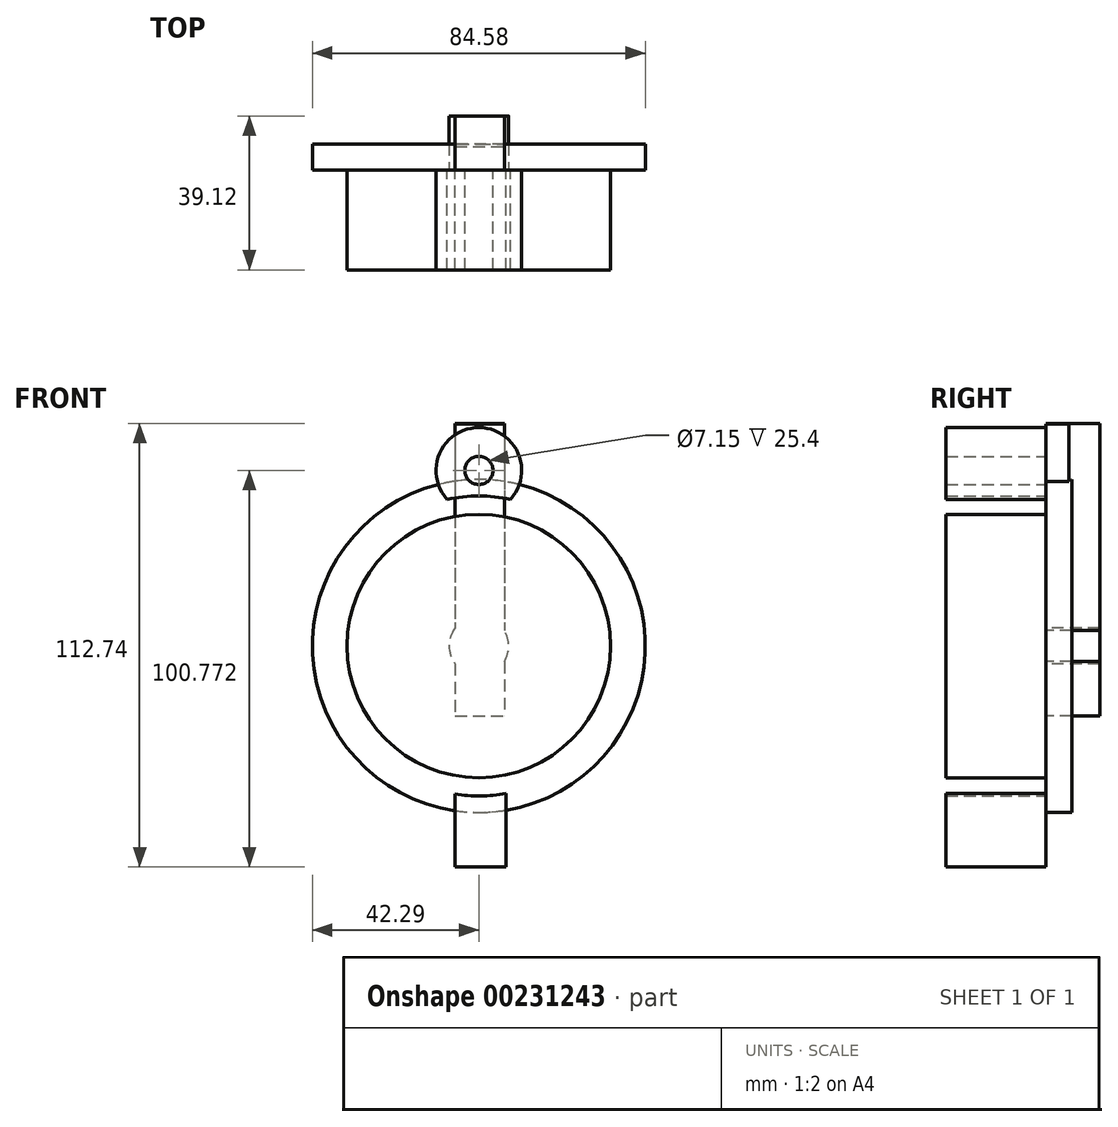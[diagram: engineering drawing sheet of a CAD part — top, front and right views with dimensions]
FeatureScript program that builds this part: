
annotation { "Feature Type Name" : "Feature", "Feature Type Description" : "" }
export const myFeature = defineFeature(function(context is Context, id is Id, definition is map)
    precondition{}
    {
        {
            var Q0;
            Q0=qCreatedBy(makeId("Front.planeOp"),FACE);
            var sketch = newSketch(context, id + "F0", { "sketchPlane" : qUnion([Q0])});
            skCircle(sketch, "E0", {"center": v(0, 0) * mm, "radius": 38.1 * mm});
            skLineSegment(sketch, "E1.bottom", {"start": v(-6.06, 0) * mm, "end": v(6.87, 0) * mm});
            skLineSegment(sketch, "E1.top", {"start": v(-6.06, -56.17) * mm, "end": v(6.87, -56.17) * mm});
            skLineSegment(sketch, "E1.left", {"start": v(-6.06, 0) * mm, "end": v(-6.06, -56.17) * mm});
            skLineSegment(sketch, "E1.right", {"start": v(6.87, 0) * mm, "end": v(6.87, -56.17) * mm});
            skCircle(sketch, "E2", {"center": v(0, 0) * mm, "radius": 33.47 * mm});
            skLineSegment(sketch, "E3", {"start": v(-8.63, 37.11) * mm, "end": v(-3.4, 33.3) * mm});
            skLineSegment(sketch, "E4", {"start": v(-3.4, 33.3) * mm, "end": v(0, 38.1) * mm});
            skLineSegment(sketch, "E5", {"start": v(0, 38.1) * mm, "end": v(4.36, 33.18) * mm});
            skLineSegment(sketch, "E6", {"start": v(4.36, 33.18) * mm, "end": v(8.75, 37.08) * mm});
            skLineSegment(sketch, "E7", {"start": v(8.75, 37.08) * mm, "end": v(10.73, 31.7) * mm});
            skLineSegment(sketch, "E8", {"start": v(10.73, 31.7) * mm, "end": v(17.4, 33.9) * mm});
            skLineSegment(sketch, "E9", {"start": v(17.4, 33.9) * mm, "end": v(17.4, 28.59) * mm});
            skLineSegment(sketch, "E10", {"start": v(17.4, 28.59) * mm, "end": v(25.19, 28.59) * mm});
            skLineSegment(sketch, "E11", {"start": v(25.19, 28.59) * mm, "end": v(23.61, 23.72) * mm});
            skLineSegment(sketch, "E12", {"start": v(23.61, 23.72) * mm, "end": v(29.81, 23.72) * mm});
            skLineSegment(sketch, "E13", {"start": v(29.81, 23.72) * mm, "end": v(27.87, 18.53) * mm});
            skLineSegment(sketch, "E14", {"start": v(27.87, 18.53) * mm, "end": v(33.29, 18.53) * mm});
            skLineSegment(sketch, "E15", {"start": v(33.29, 18.53) * mm, "end": v(30.33, 14.15) * mm});
            skLineSegment(sketch, "E16", {"start": v(30.33, 14.15) * mm, "end": v(36.34, 11.45) * mm});
            skLineSegment(sketch, "E17", {"start": v(36.34, 11.45) * mm, "end": v(32.68, 7.23) * mm});
            skLineSegment(sketch, "E18", {"start": v(32.68, 7.23) * mm, "end": v(37.97, 3.17) * mm});
            skLineSegment(sketch, "E19", {"start": v(37.97, 3.17) * mm, "end": v(33.47, 0) * mm});
            skLineSegment(sketch, "E20", {"start": v(33.47, 0) * mm, "end": v(37.64, -5.92) * mm});
            skLineSegment(sketch, "E21", {"start": v(37.64, -5.92) * mm, "end": v(32.6, -7.57) * mm});
            skLineSegment(sketch, "E22", {"start": v(32.6, -7.57) * mm, "end": v(36.02, -12.42) * mm});
            skLineSegment(sketch, "E23", {"start": v(36.02, -12.42) * mm, "end": v(30.26, -14.3) * mm});
            skLineSegment(sketch, "E24", {"start": v(30.26, -14.3) * mm, "end": v(32.23, -20.32) * mm});
            skLineSegment(sketch, "E25", {"start": v(32.23, -20.32) * mm, "end": v(26.6, -20.32) * mm});
            skLineSegment(sketch, "E26", {"start": v(26.6, -20.32) * mm, "end": v(26.6, -27.28) * mm});
            skLineSegment(sketch, "E27", {"start": v(26.6, -27.28) * mm, "end": v(21.3, -25.81) * mm});
            skLineSegment(sketch, "E28", {"start": v(21.3, -25.81) * mm, "end": v(21.3, -31.58) * mm});
            skLineSegment(sketch, "E29", {"start": v(21.3, -31.58) * mm, "end": v(17.4, -28.59) * mm});
            skLineSegment(sketch, "E30", {"start": v(17.4, -28.59) * mm, "end": v(14.09, -35.4) * mm});
            skLineSegment(sketch, "E31", {"start": v(14.09, -35.4) * mm, "end": v(11.33, -31.5) * mm});
            skLineSegment(sketch, "E32", {"start": v(11.33, -31.5) * mm, "end": v(8.95, -37.03) * mm});
            skLineSegment(sketch, "E33", {"start": v(8.95, -37.03) * mm, "end": v(4.49, -33.17) * mm});
            skLineSegment(sketch, "E34", {"start": v(4.49, -33.17) * mm, "end": v(0, -38.1) * mm});
            skLineSegment(sketch, "E35", {"start": v(0, -38.1) * mm, "end": v(-2.87, -33.35) * mm});
            skLineSegment(sketch, "E36", {"start": v(-2.87, -33.35) * mm, "end": v(-8.31, -37.18) * mm});
            skLineSegment(sketch, "E37", {"start": v(-8.31, -37.18) * mm, "end": v(-10.03, -31.93) * mm});
            skLineSegment(sketch, "E38", {"start": v(-10.03, -31.93) * mm, "end": v(-14.64, -35.17) * mm});
            skLineSegment(sketch, "E39", {"start": v(-14.64, -35.17) * mm, "end": v(-14.64, -30.1) * mm});
            skLineSegment(sketch, "E40", {"start": v(-14.64, -30.1) * mm, "end": v(-20.6, -32.05) * mm});
            skLineSegment(sketch, "E41", {"start": v(-20.6, -32.05) * mm, "end": v(-20.6, -26.38) * mm});
            skLineSegment(sketch, "E42", {"start": v(-20.6, -26.38) * mm, "end": v(-25.76, -28.07) * mm});
            skLineSegment(sketch, "E43", {"start": v(-25.76, -28.07) * mm, "end": v(-25.76, -21.37) * mm});
            skLineSegment(sketch, "E44", {"start": v(-25.76, -21.37) * mm, "end": v(-31.54, -21.37) * mm});
            skLineSegment(sketch, "E45", {"start": v(-31.54, -21.37) * mm, "end": v(-29.5, -15.83) * mm});
            skLineSegment(sketch, "E46", {"start": v(-29.5, -15.83) * mm, "end": v(-35.31, -14.3) * mm});
            skLineSegment(sketch, "E47", {"start": v(-35.31, -14.3) * mm, "end": v(-32.14, -9.34) * mm});
            skLineSegment(sketch, "E48", {"start": v(-32.14, -9.34) * mm, "end": v(-37.69, -5.6) * mm});
            skLineSegment(sketch, "E49", {"start": v(-37.69, -5.6) * mm, "end": v(-33.37, -2.57) * mm});
            skLineSegment(sketch, "E50", {"start": v(-33.37, -2.57) * mm, "end": v(-38.06, 1.63) * mm});
            skLineSegment(sketch, "E51", {"start": v(-38.06, 1.63) * mm, "end": v(-33.07, 5.15) * mm});
            skLineSegment(sketch, "E52", {"start": v(-33.07, 5.15) * mm, "end": v(-36.69, 10.28) * mm});
            skLineSegment(sketch, "E53", {"start": v(-36.69, 10.28) * mm, "end": v(-31.22, 12.08) * mm});
            skLineSegment(sketch, "E54", {"start": v(-31.22, 12.08) * mm, "end": v(-34.34, 16.5) * mm});
            skLineSegment(sketch, "E55", {"start": v(-34.34, 16.5) * mm, "end": v(-27.8, 18.65) * mm});
            skLineSegment(sketch, "E56", {"start": v(-27.8, 18.65) * mm, "end": v(-30.62, 22.67) * mm});
            skLineSegment(sketch, "E57", {"start": v(-30.62, 22.67) * mm, "end": v(-24.62, 22.67) * mm});
            skLineSegment(sketch, "E58", {"start": v(-24.62, 22.67) * mm, "end": v(-24.62, 29.08) * mm});
            skLineSegment(sketch, "E59", {"start": v(-24.62, 29.08) * mm, "end": v(-16.58, 29.08) * mm});
            skLineSegment(sketch, "E60", {"start": v(-16.58, 29.08) * mm, "end": v(-14.65, 35.17) * mm});
            skLineSegment(sketch, "E61", {"start": v(-14.65, 35.17) * mm, "end": v(-11.9, 31.28) * mm});
            skLineSegment(sketch, "E62", {"start": v(-11.9, 31.28) * mm, "end": v(-8.63, 37.11) * mm});
            skPoint(sketch, "E63.end.orphan", {"position": v(-5.46, 44.25) * mm});
            skPoint(sketch, "E64.end.orphan", {"position": v(6.93, 44.25) * mm});
            skCircle(sketch, "E65", {"center": v(0, 44.6) * mm, "radius": 10.9 * mm});
            skCircle(sketch, "E66", {"center": v(0, 44.6) * mm, "radius": 3.58 * mm});
            skSolve(sketch);
        }
        {
            var Q0;
            {var subQ5=sQuery(id+"F0.wireOp",EDGE,"E1.top");Q0=makeQuery(id+"F0.imprint","IMPRINT",FACE,{"disambiguationData":[TD([[makeQuery(id+"F0.imprint","IMPRINT",EDGE,{"derivedFrom":subQ5}),1.0]])]});}
            var Q1;
            {var subQ5=sQuery(id+"F0.wireOp",EDGE,"E1.bottom");Q1=makeQuery(id+"F0.imprint","IMPRINT",FACE,{"disambiguationData":[TD([[makeQuery(id+"F0.imprint","IMPRINT",EDGE,{"derivedFrom":subQ5}),-1.0]])]});}
            var Q2;
            {var subQ5=sQuery(id+"F0.wireOp",EDGE,"E1.bottom");Q2=makeQuery(id+"F0.imprint","IMPRINT",FACE,{"disambiguationData":[TD([[makeQuery(id+"F0.imprint","IMPRINT",EDGE,{"derivedFrom":subQ5}),1.0]])]});}
            var Q3;
            Q3=makeQuery(id+"F0.imprint","IMPRINT",FACE,{"disambiguationData":[TD([[makeQuery(id+"F0.imprint","IMPRINT",EDGE,{"derivedFrom":sQuery(id+"F0.wireOp",EDGE,"CHmG4rNv-3Th5-Iquq-n78B-wOcN8oiSMWzU")}),1.0]])]});
            var Q4;
            {var subQ0=sQuery(id+"F0.wireOp",EDGE,"E0");var subQ2=sQuery(id+"F0.wireOp",EDGE,"E65");var subQ3=makeQuery(id+"F0.imprint","INTERSECT",VERTEX,{"disambiguationData":[OD(0.0)],"derivedFrom":[subQ0,subQ2]});Q4=makeQuery(id+"F0.imprint","IMPRINT",FACE,{"disambiguationData":[TD([[makeQuery(id+"F0.imprint","IMPRINT",EDGE,{"disambiguationData":[TD([[subQ3,-1.0]])],"derivedFrom":subQ2}),1.0]])]});}
            extrude(context, id + "F1", {"entities" : qUnion([Q0, Q1, Q2, Q3, Q4]), "depth" : 25.4 * mm});
        }
        {
            var Q0;
            Q0=qCreatedBy(makeId("Front.planeOp"),FACE);
            var sketch = newSketch(context, id + "F2", { "sketchPlane" : qUnion([Q0])});
            skCircle(sketch, "E67", {"center": v(0, 0) * mm, "radius": 42.29 * mm});
            skLineSegment(sketch, "E68.bottom", {"start": v(5.44, 41.94) * mm, "end": v(-4.85, 41.94) * mm});
            skLineSegment(sketch, "E68.top", {"start": v(5.44, 15.15) * mm, "end": v(-4.85, 15.15) * mm});
            skLineSegment(sketch, "E68.left", {"start": v(5.44, 41.94) * mm, "end": v(5.44, 15.15) * mm});
            skLineSegment(sketch, "E68.right", {"start": v(-4.85, 41.94) * mm, "end": v(-4.85, 15.15) * mm});
            skSolve(sketch);
        }
        {
            var Q0;
            Q0 = qSketchRegion(id + "F2", true);
            extrude(context, id + "F3", {"entities" : qUnion([Q0]), "operationType" : NewBodyOperationType.ADD, "oppositeDirection" : true, "depth" : 6.6 * mm});
        }
        {
            var Q0;
            Q0=qCreatedBy(makeId("Top.planeOp"),FACE);
            var sketch = newSketch(context, id + "F4", { "sketchPlane" : qUnion([Q0])});
            skLineSegment(sketch, "E69.bottom", {"start": v(-6.06, 5.86) * mm, "end": v(6.47, 5.86) * mm});
            skLineSegment(sketch, "E69.top", {"start": v(-6.06, 0) * mm, "end": v(6.47, 0) * mm});
            skLineSegment(sketch, "E69.left", {"start": v(-6.06, 5.86) * mm, "end": v(-6.06, 0) * mm});
            skLineSegment(sketch, "E69.right", {"start": v(6.47, 5.86) * mm, "end": v(6.47, 0) * mm});
            skSolve(sketch);
        }
        {
            var Q0;
            Q0 = qSketchRegion(id + "F4", true);
            extrude(context, id + "F5", {"entities" : qUnion([Q0]), "operationType" : NewBodyOperationType.ADD, "depth" : 56.4 * mm});
        }
        {
            var Q0;
            Q0=qCreatedBy(makeId("Front.planeOp"),FACE);
            var sketch = newSketch(context, id + "F6", { "sketchPlane" : qUnion([Q0])});
            skCircle(sketch, "E70", {"center": v(0, 0) * mm, "radius": 7.57 * mm});
            skLineSegment(sketch, "E71", {"start": v(6.47, 56.57) * mm, "end": v(6.47, -17.78) * mm});
            skLineSegment(sketch, "E72", {"start": v(6.47, 56.57) * mm, "end": v(-6.06, 56.57) * mm});
            skLineSegment(sketch, "E73", {"start": v(-6.06, 56.57) * mm, "end": v(-6.06, -17.78) * mm});
            skLineSegment(sketch, "E74", {"start": v(-6.06, -17.78) * mm, "end": v(6.47, -17.78) * mm});
            skSolve(sketch);
        }
        {
            var Q0;
            Q0 = qSketchRegion(id + "F6", true);
            extrude(context, id + "F7", {"entities" : qUnion([Q0]), "oppositeDirection" : true, "depth" : 13.72 * mm});
        }
    });
